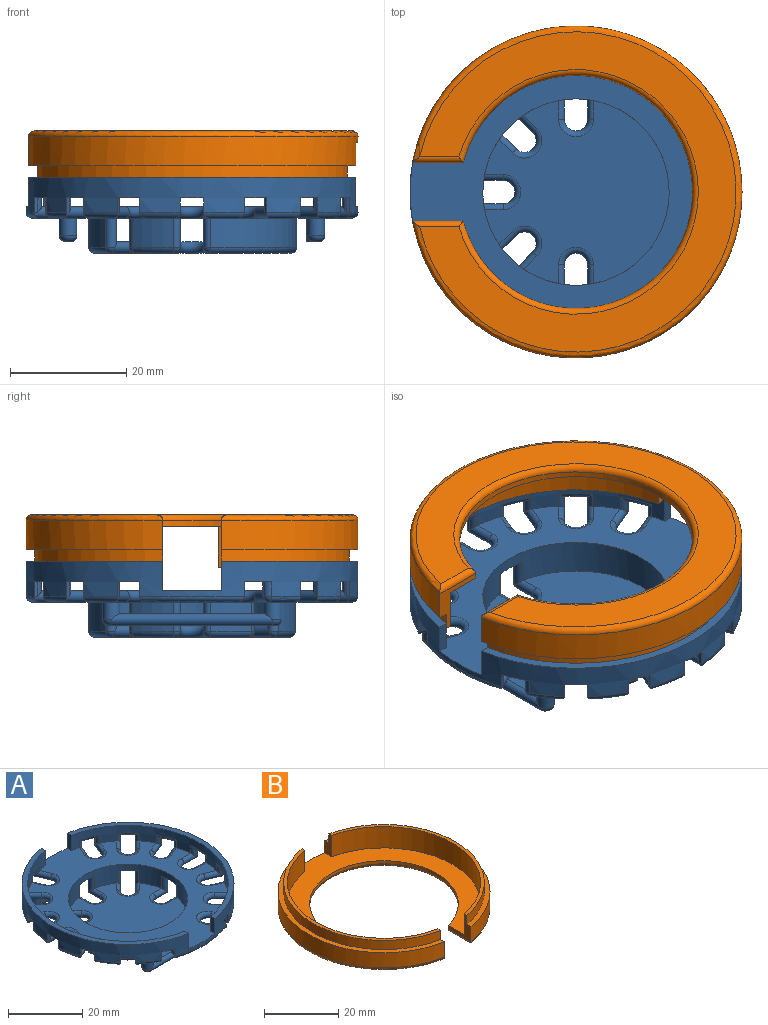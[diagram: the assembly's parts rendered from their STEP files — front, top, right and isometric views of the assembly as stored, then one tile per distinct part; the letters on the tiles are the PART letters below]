
ASSEMBLY  parts=2 mates=1
PART A: 217 faces, bbox 57.8x61.7x13 mm
  f0: cylinder r=28.5mm len=57mm, axis (0,0,-1), area 831mm2, adj f3,f4,f15,f16,f17,f18,f19,f20
  f1: cylinder r=27mm len=53.07mm, axis (0,0,1), area 272.4mm2, adj f3,f15,f68,f70,f119,f120,f122,f123
  f2: cylinder r=27mm len=53.07mm, axis (0,0,1), area 279.7mm2, adj f4,f15,f23,f47,f69,f71,f153,f155
  f3: plane 56.12x23.5mm, normal (0,0,1), area 115.7mm2, adj f0,f1,f68,f70
  f4: plane 56.12x23.5mm, normal (0,0,1), area 115.7mm2, adj f0,f2,f69,f71
  f5: cylinder r=1.5mm len=3mm, axis (0,0,1), area 24.3mm2, adj f14,f66,f67,f75,f77
  f6: cylinder r=18mm len=7.11mm, axis (0,0,1), area 38.8mm2, adj f14,f104,f109,f112
  f7: cylinder r=18mm len=7.11mm, axis (0,0,1), area 38.8mm2, adj f14,f88,f93,f94
  f8: cylinder r=18mm len=7.11mm, axis (0,0,1), area 38.8mm2, adj f14,f79,f82,f83
  f9: cylinder r=18mm len=35.44mm, axis (0,0,1), area 250.8mm2, adj f14,f90,f98,f99
  f10: cylinder r=18mm len=7.11mm, axis (0,0,1), area 38.8mm2, adj f14,f106,f113,f115
  f11: plane 33.73x33.47mm, normal (0,0,-1), area 704.9mm2, adj f81,f83,f84,f85,f87,f89,f91,f93
  f12: plane 31.72x31.43mm, normal (0,0,1), area 631.4mm2, adj f13,f81,f84,f85,f87,f89,f91,f97
  f13: cylinder r=16mm len=32mm, axis (0,0,1), area 489.7mm2, adj f12,f14,f15,f79,f81,f82,f85,f87
  f14: plane 55x54.67mm, normal (0,0,-1), area 817.9mm2, adj f5,f6,f7,f8,f9,f10,f13,f58
  f15: plane 57x53.67mm, normal (0,0,1), area 1001.8mm2, adj f0,f1,f2,f13,f68,f69,f70,f71
  f16: plane 2.5x0.59mm, normal (0,1,0), area 1.5mm2, adj f0,f44,f193,f195,f196
  f17: plane 2.5x0.59mm, normal (0,-1,0), area 1.5mm2, adj f0,f44,f195,f200,f205
  f18: plane 2.5x0.55mm, normal (-0.38,-0.92,0), area 1.5mm2, adj f0,f45,f210,f213,f216
  f19: plane 2.5x0.55mm, normal (0.38,0.92,0), area 1.5mm2, adj f0,f45,f208,f210,f211
  f20: plane 2.5x0.42mm, normal (-0.71,-0.71,0), area 1.5mm2, adj f0,f46,f199,f203,f204
  f21: plane 2.5x0.42mm, normal (0.71,0.71,0), area 1.5mm2, adj f0,f46,f204,f207,f209
  f22: plane 2.5x0.55mm, normal (-0.92,-0.38,0), area 1.5mm2, adj f0,f47,f182,f187
  f23: plane 2.5x0.38mm, normal (0.92,0.38,0), area 1mm2, adj f2,f47,f192,f194
  f24: plane 2.5x0.55mm, normal (-0.92,0.38,0), area 1.5mm2, adj f0,f48,f168,f173,f174
  f25: plane 2.5x0.55mm, normal (0.92,-0.38,0), area 1.5mm2, adj f0,f48,f174,f178,f180
  f26: plane 2.5x0.42mm, normal (-0.71,0.71,0), area 1.5mm2, adj f0,f49,f154,f159,f160
  f27: plane 2.5x0.42mm, normal (0.71,-0.71,0), area 1.5mm2, adj f0,f49,f160,f164,f166
  f28: plane 2.5x0.55mm, normal (-0.38,0.92,0), area 1.5mm2, adj f0,f50,f140,f145,f146
  f29: plane 2.5x0.55mm, normal (0.38,-0.92,0), area 1.5mm2, adj f0,f50,f146,f150,f152
  f30: plane 2.5x0.59mm, normal (0,1,0), area 1.5mm2, adj f0,f51,f126,f131,f132
  f31: plane 2.5x0.59mm, normal (0,-1,0), area 1.5mm2, adj f0,f51,f132,f136,f138
  f32: plane 2.5x0.55mm, normal (0.38,0.92,0), area 1.5mm2, adj f0,f52,f119,f120,f123
  f33: plane 2.5x0.55mm, normal (-0.38,-0.92,0), area 1.5mm2, adj f0,f52,f119,f122,f124
  f34: plane 2.5x0.42mm, normal (0.71,0.71,0), area 1.5mm2, adj f0,f53,f127,f133,f137
  f35: plane 2.5x0.42mm, normal (-0.71,-0.71,0), area 1.5mm2, adj f0,f53,f125,f127,f128
  f36: plane 2.5x0.55mm, normal (0.92,0.38,0), area 1.5mm2, adj f0,f54,f141,f147,f151
  f37: plane 2.5x0.55mm, normal (-0.92,-0.38,0), area 1.5mm2, adj f0,f54,f139,f141,f142
  f38: plane 2.5x0.55mm, normal (0.92,-0.38,0), area 1.5mm2, adj f0,f55,f155,f161,f165
  f39: plane 2.5x0.55mm, normal (-0.92,0.38,0), area 1.5mm2, adj f0,f55,f153,f155,f156
  f40: plane 2.5x0.42mm, normal (0.71,-0.71,0), area 1.5mm2, adj f0,f56,f169,f175,f179
  f41: plane 2.5x0.42mm, normal (-0.71,0.71,0), area 1.5mm2, adj f0,f56,f167,f169,f170
  f42: plane 2.5x0.55mm, normal (-0.38,0.92,0), area 1.5mm2, adj f0,f57,f181,f183,f184
  f43: plane 2.5x0.55mm, normal (0.38,-0.92,0), area 1.5mm2, adj f0,f57,f183,f188,f191
  f44: plane 4x0.57mm, normal (0,0,-1), area 2mm2, adj f0,f16,f17,f195
  f45: plane 3.89x1.99mm, normal (0,0,-1), area 2mm2, adj f0,f18,f19,f210
  f46: plane 3.18x3.18mm, normal (0,0,-1), area 2mm2, adj f0,f20,f21,f204
  f47: plane 6.11x2.92mm, normal (0,0,-1), area 6.4mm2, adj f0,f2,f22,f23,f182,f194
  f48: plane 3.89x1.99mm, normal (0,0,-1), area 2mm2, adj f0,f24,f25,f174
  f49: plane 3.18x3.18mm, normal (0,0,-1), area 2mm2, adj f0,f26,f27,f160
  f50: plane 3.89x1.99mm, normal (0,0,-1), area 2mm2, adj f0,f28,f29,f146
  f51: plane 4x0.57mm, normal (0,0,-1), area 2mm2, adj f0,f30,f31,f132
  f52: plane 3.89x1.99mm, normal (0,0,-1), area 2mm2, adj f0,f32,f33,f119
  f53: plane 3.18x3.18mm, normal (0,0,-1), area 2mm2, adj f0,f34,f35,f127
  f54: plane 3.89x1.99mm, normal (0,0,-1), area 2mm2, adj f0,f36,f37,f141
  f55: plane 3.89x1.99mm, normal (0,0,-1), area 2mm2, adj f0,f38,f39,f155
  f56: plane 3.18x3.18mm, normal (0,0,-1), area 2mm2, adj f0,f40,f41,f169
  f57: plane 3.89x1.99mm, normal (0,0,-1), area 2mm2, adj f0,f42,f43,f183
  f58: cylinder r=1.5mm len=3mm, axis (0,0,1), area 24.3mm2, adj f14,f64,f65,f72,f73
  f59: plane 29.84x2.07mm, normal (0,0,-1), area 32mm2, adj f60,f72,f73,f74
  f60: cylinder r=1.5mm len=4mm, axis (0,0,1), area 29.6mm2, adj f14,f59,f63,f64,f65,f72,f74
  f61: cylinder r=1.5mm len=3mm, axis (0,0,1), area 24.3mm2, adj f14,f66,f67,f75,f76
  f62: plane 28.73x1mm, normal (0,0,-1), area 28.5mm2, adj f75,f76,f77,f78
  f63: plane 0.74x0.07mm, normal (1,0,0), area 0mm2, adj f60,f72
  f64: plane 27.38x2mm, normal (0,0,1), area 50.6mm2, adj f58,f60,f65,f72
  f65: plane 27.38x1mm, normal (0,1,0), area 27.4mm2, adj f58,f60,f64,f74
  f66: plane 27.73x2mm, normal (0,0,1), area 50.5mm2, adj f5,f61,f67,f75
  f67: plane 27.73x1mm, normal (0,-1,0), area 27.7mm2, adj f5,f61,f66,f78
  f68: plane 5x1.53mm, normal (-1,0,0), area 7.6mm2, adj f0,f1,f3,f15
  f69: plane 5x1.53mm, normal (1,0,0), area 7.6mm2, adj f0,f2,f4,f15
  f70: plane 5x1.53mm, normal (-1,0,0), area 7.6mm2, adj f0,f1,f3,f15
  f71: plane 5x1.53mm, normal (1,0,0), area 7.6mm2, adj f0,f2,f4,f15
  f72: cylinder r=1mm len=29.23mm, axis (1,0,0), area 86.2mm2, adj f58,f59,f60,f63,f64,f73
  f73: torus R=0.5mm, axis (0,0,1), area 5.6mm2, adj f58,f59,f72,f74
  f74: cylinder r=1mm len=27.38mm, axis (-1,0,0), area 42.2mm2, adj f59,f60,f65,f73
  f75: cylinder r=1mm len=27.73mm, axis (-1,0,0), area 84.5mm2, adj f5,f61,f62,f66,f76,f77
  f76: torus R=0.5mm, axis (0,0,1), area 5.6mm2, adj f61,f62,f75,f78
  f77: torus R=0.5mm, axis (0,0,1), area 5.6mm2, adj f5,f62,f75,f78
  f78: cylinder r=1mm len=27.73mm, axis (1,0,0), area 43.6mm2, adj f62,f67,f76,f77
  f79: cylinder r=1mm len=5mm, axis (0,0,1), area 14.9mm2, adj f8,f13,f14,f80,f81
  f80: sphere r=1mm, area 1.7mm2, adj f79,f81,f83
  f81: cylinder r=1mm len=3.7mm, axis (-0.71,-0.71,0), area 12.3mm2, adj f11,f12,f13,f79,f80,f84
  f82: cylinder r=1mm len=5mm, axis (0,0,1), area 14.9mm2, adj f8,f13,f14,f85,f86
  f83: torus R=17mm, axis (0,0,1), area 11.9mm2, adj f8,f11,f80,f86
  f84: torus R=3mm, axis (0,0,1), area 23.3mm2, adj f11,f12,f81,f87
  f85: cylinder r=1mm len=4.23mm, axis (1,0,0), area 12.3mm2, adj f11,f12,f13,f82,f86,f89
  f86: sphere r=1mm, area 1.7mm2, adj f82,f83,f85
  f87: cylinder r=1mm len=3.7mm, axis (0.71,0.71,0), area 12.3mm2, adj f11,f12,f13,f84,f88,f92
  f88: cylinder r=1mm len=5mm, axis (0,0,1), area 14.9mm2, adj f7,f13,f14,f87,f92
  f89: torus R=3mm, axis (0,0,1), area 23.3mm2, adj f11,f12,f85,f91
  f90: cylinder r=1mm len=5mm, axis (0,0,1), area 14.9mm2, adj f9,f13,f14,f91,f95
  f91: cylinder r=1mm len=4.23mm, axis (-1,0,0), area 12.3mm2, adj f11,f12,f13,f89,f90,f95
  f92: sphere r=1mm, area 1.7mm2, adj f87,f88,f93
  f93: torus R=17mm, axis (0,0,1), area 11.9mm2, adj f7,f11,f92,f96
  f94: cylinder r=1mm len=5mm, axis (0,0,1), area 14.9mm2, adj f7,f13,f14,f96,f97
  f95: sphere r=1mm, area 1.7mm2, adj f90,f91,f99
  f96: sphere r=1mm, area 1.7mm2, adj f93,f94,f97
  f97: cylinder r=1mm len=4.23mm, axis (0,-1,0), area 12.3mm2, adj f11,f12,f13,f94,f96,f100
  f98: cylinder r=1mm len=5mm, axis (0,0,1), area 14.9mm2, adj f9,f13,f14,f101,f102
  f99: torus R=17mm, axis (0,0,1), area 77.2mm2, adj f9,f11,f95,f102
  f100: torus R=3mm, axis (0,0,1), area 23.3mm2, adj f11,f12,f97,f103
  f101: cylinder r=1mm len=4.23mm, axis (-1,0,0), area 12.3mm2, adj f11,f12,f13,f98,f102,f105
  f102: sphere r=1mm, area 1.7mm2, adj f98,f99,f101
  f103: cylinder r=1mm len=4.23mm, axis (0,1,0), area 12.3mm2, adj f11,f12,f13,f100,f104,f108
  f104: cylinder r=1mm len=5mm, axis (0,0,1), area 14.9mm2, adj f6,f13,f14,f103,f108
  f105: torus R=3mm, axis (0,0,1), area 23.3mm2, adj f11,f12,f101,f107
  f106: cylinder r=1mm len=5mm, axis (0,0,1), area 14.9mm2, adj f10,f13,f14,f107,f110
  f107: cylinder r=1mm len=4.23mm, axis (1,0,0), area 12.3mm2, adj f11,f12,f13,f105,f106,f110
  f108: sphere r=1mm, area 1.7mm2, adj f103,f104,f109
  f109: torus R=17mm, axis (0,0,1), area 11.9mm2, adj f6,f11,f108,f111
  f110: sphere r=1mm, area 1.7mm2, adj f106,f107,f113
  f111: sphere r=1mm, area 1.7mm2, adj f109,f112,f114
  f112: cylinder r=1mm len=5mm, axis (0,0,1), area 14.9mm2, adj f6,f13,f14,f111,f114
  f113: torus R=17mm, axis (0,0,1), area 11.9mm2, adj f10,f11,f110,f116
  f114: cylinder r=1mm len=3.7mm, axis (0.71,-0.71,0), area 12.3mm2, adj f11,f12,f13,f111,f112,f117
  f115: cylinder r=1mm len=5mm, axis (0,0,1), area 14.9mm2, adj f10,f13,f14,f116,f118
  f116: sphere r=1mm, area 1.7mm2, adj f113,f115,f118
  f117: torus R=3mm, axis (0,0,1), area 23.3mm2, adj f11,f12,f114,f118
  f118: cylinder r=1mm len=3.7mm, axis (-0.71,0.71,0), area 12.3mm2, adj f11,f12,f13,f115,f116,f117
  f119: torus R=28mm, axis (0,0,1), area 7.2mm2, adj f1,f32,f33,f52,f120,f122
  f120: cylinder r=1mm len=3.5mm, axis (0,0,1), area 3.3mm2, adj f1,f32,f119,f123
  f121: torus R=3mm, axis (0,0,1), area 23.3mm2, adj f14,f15,f123,f124
  f122: cylinder r=1mm len=3.5mm, axis (0,0,1), area 3.3mm2, adj f1,f33,f119,f124
  f123: cylinder r=1mm len=5.23mm, axis (-0.92,0.38,0), area 14mm2, adj f1,f14,f15,f32,f120,f121,f129
  f124: cylinder r=1mm len=5.23mm, axis (0.92,-0.38,0), area 14mm2, adj f1,f14,f15,f33,f121,f122,f130
  f125: cylinder r=1mm len=3.5mm, axis (0,0,1), area 3.3mm2, adj f1,f35,f127,f128
  f126: cylinder r=1mm len=3.5mm, axis (0,0,1), area 3.3mm2, adj f1,f30,f131,f132
  f127: torus R=28mm, axis (0,0,1), area 7.2mm2, adj f1,f34,f35,f53,f125,f133
  f128: cylinder r=1mm len=4.42mm, axis (0.71,-0.71,0), area 14mm2, adj f1,f14,f15,f35,f125,f129,f134
  f129: torus R=27.5mm, axis (0,0,1), area 9.9mm2, adj f0,f14,f123,f128
  f130: torus R=27.5mm, axis (0,0,1), area 9.9mm2, adj f0,f14,f124,f131
  f131: cylinder r=1mm len=5.25mm, axis (-1,0,0), area 14mm2, adj f1,f14,f15,f30,f126,f130,f135
  f132: torus R=28mm, axis (0,0,1), area 7.2mm2, adj f1,f30,f31,f51,f126,f136
  f133: cylinder r=1mm len=3.5mm, axis (0,0,1), area 3.3mm2, adj f1,f34,f127,f137
  f134: torus R=3mm, axis (0,0,1), area 23.3mm2, adj f14,f15,f128,f137
  f135: torus R=3mm, axis (0,0,1), area 23.3mm2, adj f14,f15,f131,f138
  f136: cylinder r=1mm len=3.5mm, axis (0,0,1), area 3.3mm2, adj f1,f31,f132,f138
  f137: cylinder r=1mm len=4.42mm, axis (-0.71,0.71,0), area 14mm2, adj f1,f14,f15,f34,f133,f134,f143
  f138: cylinder r=1mm len=5.25mm, axis (1,0,0), area 14mm2, adj f1,f14,f15,f31,f135,f136,f144
  f139: cylinder r=1mm len=3.5mm, axis (0,0,1), area 3.3mm2, adj f1,f37,f141,f142
  f140: cylinder r=1mm len=3.5mm, axis (0,0,1), area 3.3mm2, adj f1,f28,f145,f146
  f141: torus R=28mm, axis (0,0,1), area 7.2mm2, adj f1,f36,f37,f54,f139,f147
  f142: cylinder r=1mm len=5.23mm, axis (0.38,-0.92,0), area 14mm2, adj f1,f14,f15,f37,f139,f143,f148
  f143: torus R=27.5mm, axis (0,0,1), area 9.9mm2, adj f0,f14,f137,f142
  f144: torus R=27.5mm, axis (0,0,1), area 9.9mm2, adj f0,f14,f138,f145
  f145: cylinder r=1mm len=5.23mm, axis (-0.92,-0.38,0), area 14mm2, adj f1,f14,f15,f28,f140,f144,f149
  f146: torus R=28mm, axis (0,0,1), area 7.2mm2, adj f1,f28,f29,f50,f140,f150
  f147: cylinder r=1mm len=3.5mm, axis (0,0,1), area 3.3mm2, adj f1,f36,f141,f151
  f148: torus R=3mm, axis (0,0,1), area 23.3mm2, adj f14,f15,f142,f151
  f149: torus R=3mm, axis (0,0,1), area 23.3mm2, adj f14,f15,f145,f152
  f150: cylinder r=1mm len=3.5mm, axis (0,0,1), area 3.3mm2, adj f1,f29,f146,f152
  f151: cylinder r=1mm len=5.23mm, axis (-0.38,0.92,0), area 14mm2, adj f1,f14,f15,f36,f147,f148,f157
  f152: cylinder r=1mm len=5.23mm, axis (0.92,0.38,0), area 14mm2, adj f1,f14,f15,f29,f149,f150,f158
  f153: cylinder r=1mm len=3.5mm, axis (0,0,1), area 3.3mm2, adj f2,f39,f155,f156
  f154: cylinder r=1mm len=3.5mm, axis (0,0,1), area 3.3mm2, adj f1,f26,f159,f160
  f155: torus R=28mm, axis (0,0,1), area 7.2mm2, adj f2,f38,f39,f55,f153,f161
  f156: cylinder r=1mm len=5.23mm, axis (-0.38,-0.92,0), area 14mm2, adj f2,f14,f15,f39,f153,f157,f162
  f157: torus R=27.5mm, axis (0,0,1), area 27.3mm2, adj f0,f14,f151,f156
  f158: torus R=27.5mm, axis (0,0,1), area 9.9mm2, adj f0,f14,f152,f159
  f159: cylinder r=1mm len=4.42mm, axis (-0.71,-0.71,0), area 14mm2, adj f1,f14,f15,f26,f154,f158,f163
  f160: torus R=28mm, axis (0,0,1), area 7.2mm2, adj f1,f26,f27,f49,f154,f164
  f161: cylinder r=1mm len=3.5mm, axis (0,0,1), area 3.3mm2, adj f2,f38,f155,f165
  f162: torus R=3mm, axis (0,0,1), area 23.3mm2, adj f14,f15,f156,f165
  f163: torus R=3mm, axis (0,0,1), area 23.3mm2, adj f14,f15,f159,f166
  f164: cylinder r=1mm len=3.5mm, axis (0,0,1), area 3.3mm2, adj f1,f27,f160,f166
  f165: cylinder r=1mm len=5.23mm, axis (0.38,0.92,0), area 14mm2, adj f2,f14,f15,f38,f161,f162,f171
  f166: cylinder r=1mm len=4.42mm, axis (0.71,0.71,0), area 14mm2, adj f1,f14,f15,f27,f163,f164,f172
  f167: cylinder r=1mm len=3.5mm, axis (0,0,1), area 3.3mm2, adj f2,f41,f169,f170
  f168: cylinder r=1mm len=3.5mm, axis (0,0,1), area 3.3mm2, adj f1,f24,f173,f174
  f169: torus R=28mm, axis (0,0,1), area 7.2mm2, adj f2,f40,f41,f56,f167,f175
  f170: cylinder r=1mm len=4.42mm, axis (-0.71,-0.71,0), area 14mm2, adj f2,f14,f15,f41,f167,f171,f176
  f171: torus R=27.5mm, axis (0,0,1), area 9.9mm2, adj f0,f14,f165,f170
  f172: torus R=27.5mm, axis (0,0,1), area 9.9mm2, adj f0,f14,f166,f173
  f173: cylinder r=1mm len=5.23mm, axis (-0.38,-0.92,0), area 14mm2, adj f1,f14,f15,f24,f168,f172,f177
  f174: torus R=28mm, axis (0,0,1), area 7.2mm2, adj f1,f24,f25,f48,f168,f178
  f175: cylinder r=1mm len=3.5mm, axis (0,0,1), area 3.3mm2, adj f2,f40,f169,f179
  f176: torus R=3mm, axis (0,0,1), area 23.3mm2, adj f14,f15,f170,f179
  f177: torus R=3mm, axis (0,0,1), area 23.3mm2, adj f14,f15,f173,f180
  f178: cylinder r=1mm len=3.5mm, axis (0,0,1), area 3.3mm2, adj f1,f25,f174,f180
  f179: cylinder r=1mm len=4.42mm, axis (0.71,0.71,0), area 14mm2, adj f2,f14,f15,f40,f175,f176,f185
  f180: cylinder r=1mm len=5.23mm, axis (0.38,0.92,0), area 14mm2, adj f1,f14,f15,f25,f177,f178,f186
  f181: cylinder r=1mm len=3.5mm, axis (0,0,1), area 3.3mm2, adj f2,f42,f183,f184
  f182: cylinder r=1mm len=2.5mm, axis (0,0,1), area 2.8mm2, adj f2,f22,f47,f187
  f183: torus R=28mm, axis (0,0,1), area 7.2mm2, adj f2,f42,f43,f57,f181,f188
  f184: cylinder r=1mm len=5.23mm, axis (-0.92,-0.38,0), area 14mm2, adj f2,f14,f15,f42,f181,f185,f189
  f185: torus R=27.5mm, axis (0,0,1), area 9.9mm2, adj f0,f14,f179,f184
  f186: torus R=27.5mm, axis (0,0,1), area 27.3mm2, adj f0,f14,f180,f187
  f187: cylinder r=1mm len=5.23mm, axis (0.38,-0.92,0), area 14mm2, adj f2,f14,f15,f22,f182,f186,f190
  f188: cylinder r=1mm len=3.5mm, axis (0,0,1), area 3.3mm2, adj f2,f43,f183,f191
  f189: torus R=3mm, axis (0,0,1), area 23.3mm2, adj f14,f15,f184,f191
  f190: torus R=3mm, axis (0,0,1), area 23.3mm2, adj f14,f15,f187,f192
  f191: cylinder r=1mm len=5.23mm, axis (0.92,0.38,0), area 14mm2, adj f2,f14,f15,f43,f188,f189,f197
  f192: cylinder r=1mm len=4.22mm, axis (-0.38,0.92,0), area 12.3mm2, adj f2,f14,f15,f23,f190,f198
  f193: cylinder r=1mm len=3.5mm, axis (0,0,1), area 3.3mm2, adj f2,f16,f195,f196
  f194: cylinder r=1mm len=2.5mm, axis (0,0,-1), area 4.2mm2, adj f0,f23,f47,f198
  f195: torus R=28mm, axis (0,0,1), area 7.2mm2, adj f2,f16,f17,f44,f193,f200
  f196: cylinder r=1mm len=5.25mm, axis (-1,0,0), area 14mm2, adj f2,f14,f15,f16,f193,f197,f201
  f197: torus R=27.5mm, axis (0,0,1), area 9.9mm2, adj f0,f14,f191,f196
  f198: sphere r=1mm, area 1.7mm2, adj f192,f194,f202
  f199: cylinder r=1mm len=3.5mm, axis (0,0,1), area 3.3mm2, adj f2,f20,f203,f204
  f200: cylinder r=1mm len=3.5mm, axis (0,0,1), area 3.3mm2, adj f2,f17,f195,f205
  f201: torus R=3mm, axis (0,0,1), area 23.3mm2, adj f14,f15,f196,f205
  f202: torus R=27.5mm, axis (0,0,1), area 8.8mm2, adj f0,f14,f198,f203
  f203: cylinder r=1mm len=4.42mm, axis (0.71,-0.71,0), area 14mm2, adj f2,f14,f15,f20,f199,f202,f206
  f204: torus R=28mm, axis (0,0,1), area 7.2mm2, adj f2,f20,f21,f46,f199,f207
  f205: cylinder r=1mm len=5.25mm, axis (1,0,0), area 14mm2, adj f2,f14,f15,f17,f200,f201,f212
  f206: torus R=3mm, axis (0,0,1), area 23.3mm2, adj f14,f15,f203,f209
  f207: cylinder r=1mm len=3.5mm, axis (0,0,1), area 3.3mm2, adj f2,f21,f204,f209
  f208: cylinder r=1mm len=3.5mm, axis (0,0,1), area 3.3mm2, adj f2,f19,f210,f211
  f209: cylinder r=1mm len=4.42mm, axis (-0.71,0.71,0), area 14mm2, adj f2,f14,f15,f21,f206,f207,f215
  f210: torus R=28mm, axis (0,0,1), area 7.2mm2, adj f2,f18,f19,f45,f208,f213
  f211: cylinder r=1mm len=5.23mm, axis (-0.92,0.38,0), area 14mm2, adj f2,f14,f15,f19,f208,f212,f214
  f212: torus R=27.5mm, axis (0,0,1), area 9.9mm2, adj f0,f14,f205,f211
  f213: cylinder r=1mm len=3.5mm, axis (0,0,1), area 3.3mm2, adj f2,f18,f210,f216
  f214: torus R=3mm, axis (0,0,1), area 23.3mm2, adj f14,f15,f211,f216
  f215: torus R=27.5mm, axis (0,0,1), area 9.9mm2, adj f0,f14,f209,f216
  f216: cylinder r=1mm len=5.23mm, axis (0.92,-0.38,0), area 14mm2, adj f2,f14,f15,f18,f213,f214,f215
PART B: 20 faces, bbox 61.7x61.2x9 mm
  f0: cylinder r=27mm len=52.97mm, axis (0,0,-1), area 222.9mm2, adj f1,f4,f13,f15
  f1: plane 52.97x22mm, normal (0,0,1), area 72.7mm2, adj f0,f2,f13,f15
  f2: cylinder r=26mm len=50.93mm, axis (0,0,1), area 498mm2, adj f1,f8,f13,f15
  f3: cylinder r=28.5mm len=57mm, axis (0,0,-1), area 804.9mm2, adj f4,f8,f11,f12,f13,f14,f15,f17
  f4: plane 56.03x23.5mm, normal (0,0,1), area 115mm2, adj f0,f3,f13,f15
  f5: cylinder r=27mm len=53.15mm, axis (0,0,-1), area 225.7mm2, adj f6,f11,f12,f14
  f6: plane 53.15x22.47mm, normal (0,0,1), area 73.7mm2, adj f5,f9,f12,f14
  f7: plane 55x54.34mm, normal (0,0,-1), area 911.6mm2, adj f16,f17,f18,f19
  f8: plane 54.01x52mm, normal (0,0,1), area 831.7mm2, adj f2,f3,f9,f10,f12,f13,f14,f15
  f9: cylinder r=26mm len=51.12mm, axis (0,0,1), area 504.7mm2, adj f6,f8,f12,f14
  f10: cylinder r=20mm len=40mm, axis (0,0,-1), area 115.6mm2, adj f8,f12,f13,f18
  f11: plane 56.2x23.97mm, normal (0,0,1), area 116.4mm2, adj f3,f5,f12,f14
  f12: plane 8.69x8mm, normal (1,0,0), area 21.9mm2, adj f3,f5,f6,f8,f9,f10,f11,f19
  f13: plane 8.69x8mm, normal (-1,0,0), area 21.9mm2, adj f0,f1,f2,f3,f4,f8,f10,f16
  f14: plane 7x2.54mm, normal (1,0,0), area 13.2mm2, adj f3,f5,f6,f8,f9,f11
  f15: plane 7x2.55mm, normal (-1,0,0), area 13.3mm2, adj f0,f1,f2,f3,f4,f8
  f16: cylinder r=1mm len=8.69mm, axis (0,-1,0), area 12.5mm2, adj f7,f13,f17,f18
  f17: torus R=27.5mm, axis (0,0,1), area 260.7mm2, adj f3,f7,f16,f19
  f18: torus R=21mm, axis (0,0,1), area 183.9mm2, adj f7,f10,f16,f19
  f19: cylinder r=1mm len=8.69mm, axis (0,1,0), area 12.5mm2, adj f7,f12,f17,f18
PLACE A rot(axis=(0,0,1),90deg) t=(46.81,-9.26,-132.67)mm
PLACE B rot(axis=(0.71,0.71,0),180deg) t=(46.81,-9.26,-117.67)mm
MATE parallel A.f0 <-> B.f0  axis (0,0,1) through (46.81,-9.26,-125.67)mm
